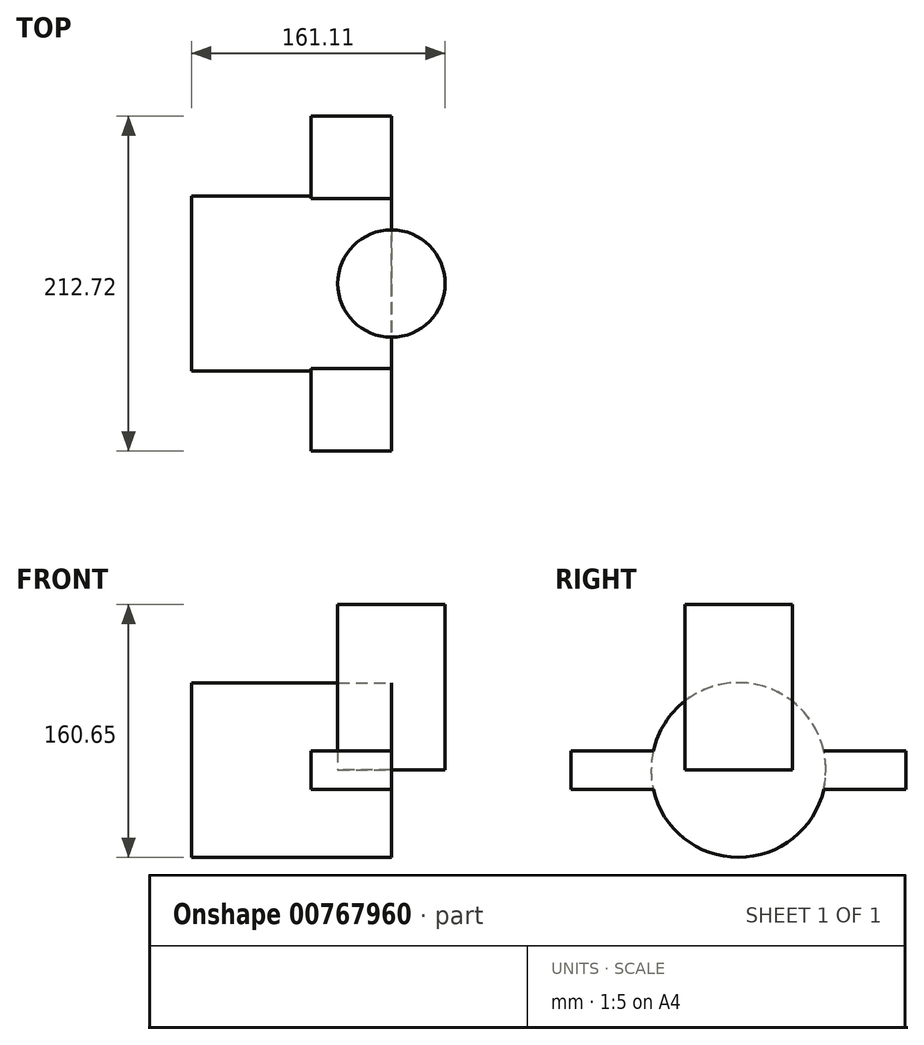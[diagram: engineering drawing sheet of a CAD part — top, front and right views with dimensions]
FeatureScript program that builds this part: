
annotation { "Feature Type Name" : "Feature", "Feature Type Description" : "" }
export const myFeature = defineFeature(function(context is Context, id is Id, definition is map)
    precondition{}
    {
        {
            var Q0;
            Q0=qCreatedBy(makeId("Right.planeOp"),FACE);
            var sketch = newSketch(context, id + "F0", { "sketchPlane" : qUnion([Q0])});
            skCircle(sketch, "E0", {"center": v(0, 0) * mm, "radius": 55.5 * mm});
            skSolve(sketch);
        }
        {
            var Q0;
            Q0=makeQuery(id+"F0.imprint","IMPRINT",FACE,{"disambiguationData":[TD([[makeQuery(id+"F0.imprint","IMPRINT",EDGE,{"derivedFrom":sQuery(id+"F0.wireOp",EDGE,"E0")}),1.0]])]});
            extrude(context, id + "F1", {"entities" : qUnion([Q0]), "oppositeDirection" : true, "depth" : 127 * mm, "offsetDistance" : 25.4 * mm});
        }
        {
            var Q0;
            Q0=makeQuery(id+"F1.opExtrude","CAP_FACE",FACE,{"disambiguationData":[OSD([sQuery(id+"F0.wireOp",EDGE,"E0")])],"isStart":true});
            var sketch = newSketch(context, id + "F2", { "sketchPlane" : qUnion([Q0])});
            skLineSegment(sketch, "E1.bottom", {"start": v(-106.36, 12.28) * mm, "end": v(106.36, 12.28) * mm});
            skLineSegment(sketch, "E1.top", {"start": v(-106.36, -12.28) * mm, "end": v(106.36, -12.28) * mm});
            skLineSegment(sketch, "E1.left", {"start": v(-106.36, 12.28) * mm, "end": v(-106.36, -12.28) * mm});
            skLineSegment(sketch, "E1.right", {"start": v(106.36, 12.28) * mm, "end": v(106.36, -12.28) * mm});
            skPoint(sketch, "E1.middle", {"position": v(0, 0) * mm});
            skSolve(sketch);
        }
        {
            var Q0;
            {var subQ0=sQuery(id+"F2.wireOp",EDGE,"E1.left");Q0=makeQuery(id+"F2.imprint","IMPRINT",FACE,{"disambiguationData":[TD([[makeQuery(id+"F2.imprint","IMPRINT",EDGE,{"derivedFrom":subQ0}),1.0]])]});}
            var Q1;
            {var subQ0=sQuery(id+"F2.wireOp",EDGE,"E1.bottom");var subQ1=makeQuery(id+"F1.opExtrude","CAP_EDGE",EDGE,{"disambiguationData":[OSD([sQuery(id+"F0.wireOp",EDGE,"E0")])],"isStart":true});var subQ2=makeQuery(id+"F2.imprint","INTERSECT",VERTEX,{"disambiguationData":[OD(0.0)],"derivedFrom":[subQ1,subQ0]});Q1=makeQuery(id+"F2.imprint","IMPRINT",FACE,{"disambiguationData":[TD([[makeQuery(id+"F2.imprint","IMPRINT",EDGE,{"disambiguationData":[TD([[subQ2,-1.0]])],"derivedFrom":subQ0}),-1.0]])]});}
            var Q2;
            {var subQ0=sQuery(id+"F2.wireOp",EDGE,"E1.right");Q2=makeQuery(id+"F2.imprint","IMPRINT",FACE,{"disambiguationData":[TD([[makeQuery(id+"F2.imprint","IMPRINT",EDGE,{"derivedFrom":subQ0}),-1.0]])]});}
            extrude(context, id + "F3", {"entities" : qUnion([Q0, Q1, Q2]), "operationType" : NewBodyOperationType.ADD, "oppositeDirection" : true, "depth" : 51.05 * mm, "offsetDistance" : 25.4 * mm});
        }
        {
            var Q0;
            Q0=qCreatedBy(makeId("Top.planeOp"),FACE);
            var sketch = newSketch(context, id + "F4", { "sketchPlane" : qUnion([Q0])});
            skCircle(sketch, "E2", {"center": v(0, 0) * mm, "radius": 34.11 * mm});
            skSolve(sketch);
        }
        {
            var Q0;
            Q0=makeQuery(id+"F4.imprint","IMPRINT",FACE,{"disambiguationData":[TD([[makeQuery(id+"F4.imprint","IMPRINT",EDGE,{"derivedFrom":sQuery(id+"F4.wireOp",EDGE,"E2")}),1.0]])]});
            extrude(context, id + "F5", {"entities" : qUnion([Q0]), "depth" : 105.16 * mm, "offsetDistance" : 25.4 * mm});
        }
    });
